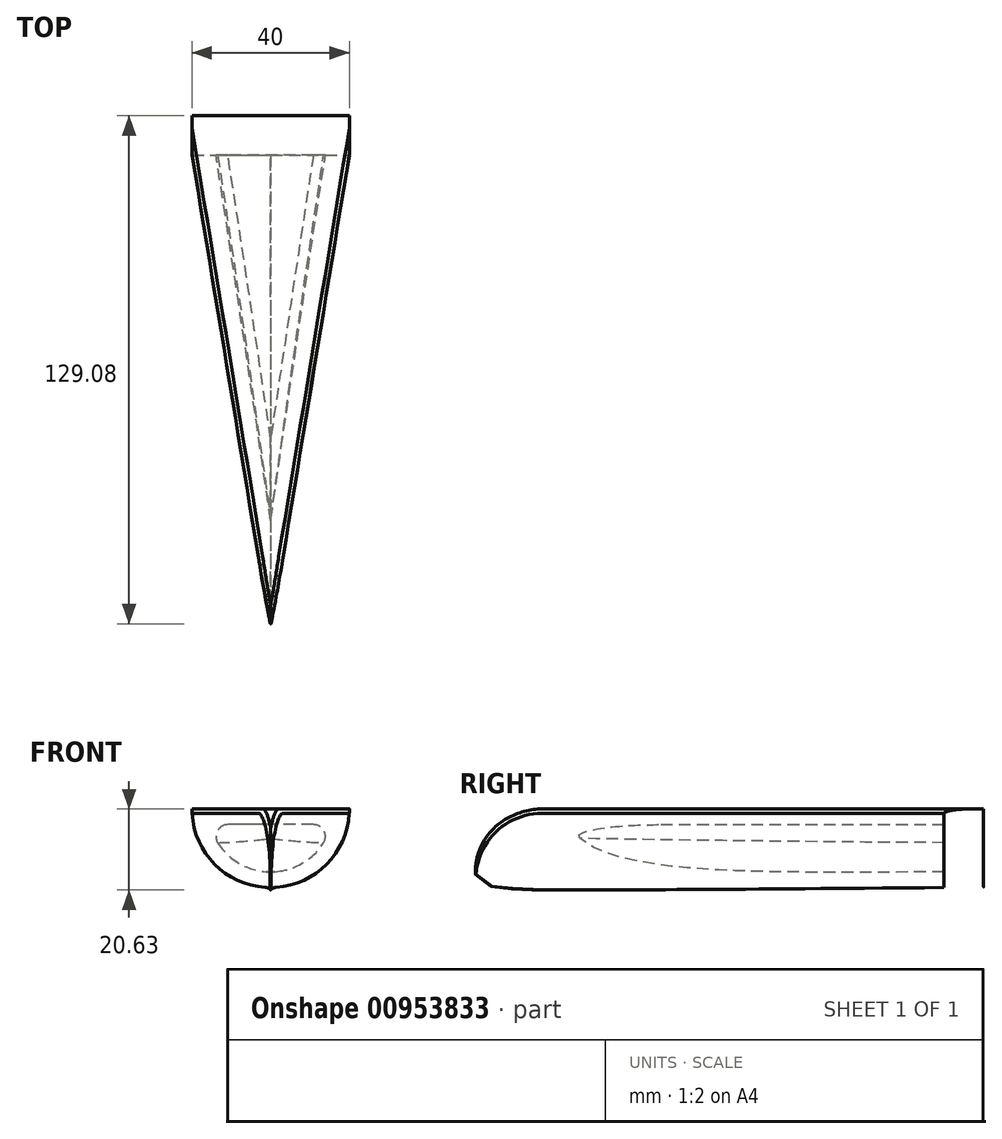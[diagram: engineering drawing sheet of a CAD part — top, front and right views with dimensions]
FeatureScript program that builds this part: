
annotation { "Feature Type Name" : "Feature", "Feature Type Description" : "" }
export const myFeature = defineFeature(function(context is Context, id is Id, definition is map)
    precondition{}
    {
        {
            var Q0;
            Q0=qCreatedBy(makeId("Front.planeOp"),FACE);
            var sketch = newSketch(context, id + "F0", { "sketchPlane" : qUnion([Q0])});
            skArc(sketch, "E0", {"start": v(20, 0) * mm, "mid": v(0, -20) * mm, "end": v(-20, 0) * mm});
            skLineSegment(sketch, "E1", {"start": v(20, 0) * mm, "end": v(-20, 0) * mm});
            skLineSegment(sketch, "E2", {"start": v(0, 0) * mm, "end": v(0, -20) * mm});
            skSolve(sketch);
        }
        {
            var Q0;
            Q0=qCreatedBy(makeId("Front.planeOp"),FACE);
            cPlane(context, id + "F1", {"entities" : qUnion([Q0]), "cplaneType" : CPlaneType.OFFSET, "offset" : 120 * mm, "width" : 150 * mm, "height" : 150 * mm});
        }
        {
            var Q0;
            Q0=qCreatedBy(id+"F1.planeOp",FACE);
            var sketch = newSketch(context, id + "F2", { "sketchPlane" : qUnion([Q0])});
            skLineSegment(sketch, "E3", {"start": v(0, 0) * mm, "end": v(0.2, 0) * mm});
            skLineSegment(sketch, "E4", {"start": v(0, 0) * mm, "end": v(-0.2, 0) * mm});
            skLineSegment(sketch, "E5", {"start": v(0, 0) * mm, "end": v(0, -21) * mm});
            skLineSegment(sketch, "E6", {"start": v(-0.2, 0) * mm, "end": v(0, -21) * mm});
            skLineSegment(sketch, "E7", {"start": v(0.2, 0) * mm, "end": v(0, -21) * mm});
            skSolve(sketch);
        }
        {
            var Q0;
            {var subQ3=sQuery(id+"F0.wireOp",EDGE,"E2");Q0=makeQuery(id+"F0.imprint","IMPRINT",FACE,{"disambiguationData":[TD([[makeQuery(id+"F0.imprint","IMPRINT",EDGE,{"derivedFrom":subQ3}),-1.0]])]});}
            var Q1;
            Q1=makeQuery(id+"F2.imprint","IMPRINT",FACE,{"disambiguationData":[TD([[makeQuery(id+"F2.imprint","IMPRINT",EDGE,{"derivedFrom":sQuery(id+"F2.wireOp",EDGE,"E4")}),1.0]])]});
            loft(context, id + "F3", {"sheetProfilesArray" : [{ "sheetProfileEntities" : qUnion([Q0]) }, { "sheetProfileEntities" : qUnion([Q1]) }]});
        }
        {
            var Q1;
            {var subQ3=sQuery(id+"F0.wireOp",EDGE,"E2");Q1=makeQuery(id+"F0.imprint","IMPRINT",FACE,{"disambiguationData":[TD([[makeQuery(id+"F0.imprint","IMPRINT",EDGE,{"derivedFrom":subQ3}),1.0]])]});}
            var Q2;
            Q2=makeQuery(id+"F2.imprint","IMPRINT",FACE,{"disambiguationData":[TD([[makeQuery(id+"F2.imprint","IMPRINT",EDGE,{"derivedFrom":sQuery(id+"F2.wireOp",EDGE,"E3")}),-1.0]])]});
            loft(context, id + "F4", {"operationType" : NewBodyOperationType.ADD, "sheetProfilesArray" : [{ "sheetProfileEntities" : qUnion([Q1]) }, { "sheetProfileEntities" : qUnion([Q2]) }]});
        }
        {
            var Q0;
            {var subQ0=sQuery(id+"F2.wireOp",EDGE,"E5");var subQ1=sQuery(id+"F2.wireOp",EDGE,"E4");var subQ2=sQuery(id+"F2.wireOp",EDGE,"E3");Q0=makeQuery(id+"F4.boolean.opBoolean","MERGE",EDGE,{"derivedFrom":[makeQuery(id+"F3.opLoft","MID_CAP_EDGE",EDGE,{"disambiguationData":[OSD([subQ2,subQ1,subQ0,sQuery(id+"F2.wireOp",EDGE,"E6")])],"capPos":1.0}),makeQuery(id+"F4.opLoft","MID_CAP_EDGE",EDGE,{"disambiguationData":[OSD([subQ2,subQ1,subQ0,sQuery(id+"F2.wireOp",EDGE,"E7")])],"capPos":1.0})]});}
            fillet(context, id + "F5", {"entities" : qUnion([Q0]), "radius" : 18 * mm, "tangentPropagation" : true, "allowEdgeOverflow" : false});
        }
        {
            var Q0;
            {var subQ0=sQuery(id+"F2.wireOp",EDGE,"E7");var subQ1=sQuery(id+"F2.wireOp",EDGE,"E6");var subQ2=sQuery(id+"F2.wireOp",EDGE,"E5");var subQ3=sQuery(id+"F0.wireOp",EDGE,"E2");var subQ4=sQuery(id+"F0.wireOp",EDGE,"E0");Q0=makeQuery(id+"F4.boolean.opBoolean","MERGE",EDGE,{"derivedFrom":[makeQuery(id+"F3.opLoft","SWEPT_EDGE",EDGE,{"disambiguationData":[OSD([subQ4,subQ3,subQ2,subQ1,subQ0])]}),makeQuery(id+"F4.opLoft","SWEPT_EDGE",EDGE,{"disambiguationData":[OSD([subQ4,subQ3,subQ2,subQ1,subQ0])]})]});}
            fillet(context, id + "F6", {"entities" : qUnion([Q0]), "radius" : 0.1 * mm, "tangentPropagation" : true, "allowEdgeOverflow" : false});
        }
        {
            var Q0;
            {var subQ3=sQuery(id+"F0.wireOp",EDGE,"E2");var subQ6=makeQuery(id+"F0.imprint","IMPRINT",EDGE,{"derivedFrom":subQ3});Q0=makeQuery(id+"F4.boolean.opBoolean","MERGE",FACE,{"derivedFrom":[makeQuery(id+"F3.opLoft","CAP_FACE",FACE,{"disambiguationData":[OSD([makeQuery(id+"F0.imprint","IMPRINT",FACE,{"disambiguationData":[TD([[subQ6,-1.0]])]})])],"isStart":true}),makeQuery(id+"F4.opLoft","CAP_FACE",FACE,{"disambiguationData":[OSD([makeQuery(id+"F0.imprint","IMPRINT",FACE,{"disambiguationData":[TD([[subQ6,1.0]])]})])],"isStart":true})]});}
            shell(context, id + "F7", {"entities" : qUnion([Q0]), "thickness" : 4 * mm});
        }
        {
            var Q0;
            Q0=makeQuery(id+"F7.opShell","OFFSET_EDGE",EDGE,{"disambiguationData":[OSD([sQuery(id+"F0.wireOp",EDGE,"E0"),sQuery(id+"F0.wireOp",EDGE,"E1"),sQuery(id+"F2.wireOp",EDGE,"E3"),sQuery(id+"F2.wireOp",EDGE,"E7")])]});
            var Q1;
            Q1=makeQuery(id+"F7.opShell","OFFSET_EDGE",EDGE,{"disambiguationData":[OSD([sQuery(id+"F0.wireOp",EDGE,"E0"),sQuery(id+"F0.wireOp",EDGE,"E1"),sQuery(id+"F2.wireOp",EDGE,"E4"),sQuery(id+"F2.wireOp",EDGE,"E6")])]});
            fillet(context, id + "F8", {"entities" : qUnion([Q0, Q1]), "radius" : 3 * mm, "tangentPropagation" : true, "allowEdgeOverflow" : false});
        }
        {
            var Q0;
            Q0=qCreatedBy(makeId("Front.planeOp"),FACE);
            var sketch = newSketch(context, id + "F9", { "sketchPlane" : qUnion([Q0])});
            skArc(sketch, "E8", {"start": v(-20, 0) * mm, "mid": v(0, -20) * mm, "end": v(20, 0) * mm});
            skLineSegment(sketch, "E9", {"start": v(20, 0) * mm, "end": v(-20, 0) * mm});
            skSolve(sketch);
        }
        {
            var Q0;
            Q0 = qSketchRegion(id + "F9", true);
            extrude(context, id + "F10", {"entities" : qUnion([Q0]), "operationType" : NewBodyOperationType.ADD, "oppositeDirection" : true, "depth" : 10 * mm, "offsetDistance" : 25 * mm});
        }
        {
            var Q0;
            {var subQ0=sQuery(id+"F2.wireOp",EDGE,"E7");var subQ1=sQuery(id+"F2.wireOp",EDGE,"E6");var subQ2=sQuery(id+"F2.wireOp",EDGE,"E5");var subQ3=sQuery(id+"F2.wireOp",EDGE,"E4");var subQ4=sQuery(id+"F2.wireOp",EDGE,"E3");Q0=makeQuery(id+"F5.opFillet","BLEND_EDGE",EDGE,{"blendedFrom":[makeQuery(id+"F4.boolean.opBoolean","MERGE",EDGE,{"derivedFrom":[makeQuery(id+"F3.opLoft","MID_CAP_EDGE",EDGE,{"disambiguationData":[OSD([subQ4,subQ3,subQ2,subQ1])],"capPos":1.0}),makeQuery(id+"F4.opLoft","MID_CAP_EDGE",EDGE,{"disambiguationData":[OSD([subQ4,subQ3,subQ2,subQ0])],"capPos":1.0})]}),makeQuery(id+"F3.opLoft","SWEPT_FACE",FACE,{"disambiguationData":[OSD([sQuery(id+"F0.wireOp",EDGE,"E0"),sQuery(id+"F0.wireOp",EDGE,"E1"),sQuery(id+"F0.wireOp",EDGE,"E2"),subQ3,subQ2,subQ1,subQ0])]})],"blendedInto":[makeQuery(id+"F3.opLoft","SWEPT_FACE",FACE,{"disambiguationData":[OSD([sQuery(id+"F0.wireOp",EDGE,"E0"),sQuery(id+"F0.wireOp",EDGE,"E1"),sQuery(id+"F0.wireOp",EDGE,"E2"),subQ3,subQ2,subQ1,subQ0])]})]});}
            fillet(context, id + "F11", {"entities" : qUnion([Q0]), "radius" : 1.1 * mm, "tangentPropagation" : true, "allowEdgeOverflow" : false});
        }
    });
